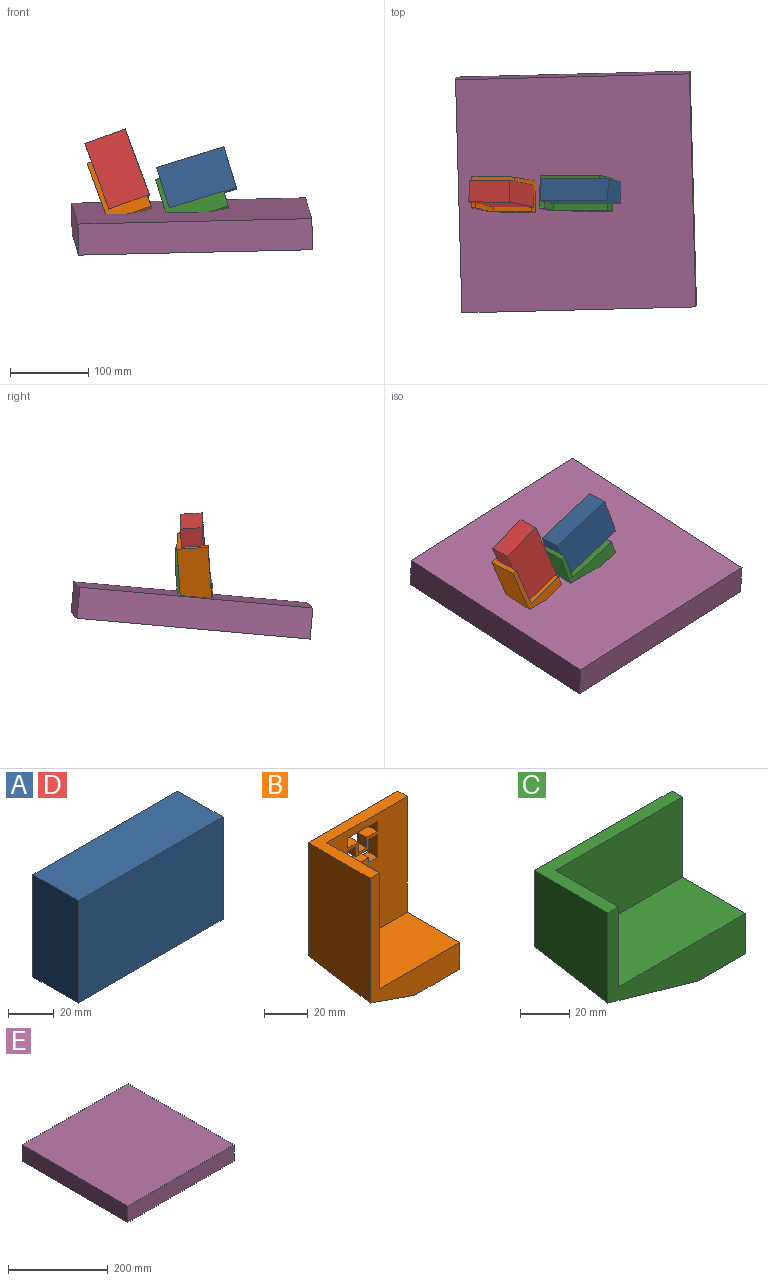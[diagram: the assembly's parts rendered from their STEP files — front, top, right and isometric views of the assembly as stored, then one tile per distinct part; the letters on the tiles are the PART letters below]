
ASSEMBLY  parts=5 mates=4
PART A: 6 faces, bbox 90x28x55 mm
  f0: plane 90x28mm, normal (0,0,1), area 2520mm2, adj f1,f3,f4,f5
  f1: plane 55x28mm, normal (-1,0,0), area 1540mm2, adj f0,f2,f4,f5
  f2: plane 90x28mm, normal (0,0,-1), area 2520mm2, adj f1,f3,f4,f5
  f3: plane 55x28mm, normal (1,0,0), area 1540mm2, adj f0,f2,f4,f5
  f4: plane 90x55mm, normal (0,-1,0), area 4950mm2, adj f0,f1,f2,f3
  f5: plane 90x55mm, normal (0,1,0), area 4950mm2, adj f0,f1,f2,f3
PART B: 30 faces, bbox 58x40x80 mm
  f0: plane 80x58mm, normal (0,1,0), area 3928.8mm2, adj f3,f4,f5,f6,f9,f10,f11,f12
  f1: plane 65x52mm, normal (0,-1,0), area 3062.6mm2, adj f5,f6,f7,f8,f10,f11,f12,f13
  f2: plane 80x58mm, normal (0,-1,0), area 1114.5mm2, adj f3,f4,f5,f6,f7,f8,f9
  f3: plane 69.92x40mm, normal (-1,0,0), area 2666.6mm2, adj f0,f2,f6,f9
  f4: plane 40x29.14mm, normal (0,0,-1), area 793mm2, adj f0,f2,f5,f9
  f5: plane 80x40mm, normal (1,0,0), area 990mm2, adj f0,f1,f2,f4,f6,f8
  f6: plane 58x40mm, normal (0,0,1), area 552mm2, adj f0,f1,f2,f3,f5,f7
  f7: plane 65x34mm, normal (1,0,0), area 2210mm2, adj f1,f2,f6,f8
  f8: plane 52x34mm, normal (0,0,1), area 1768mm2, adj f1,f2,f5,f7
  f9: plane 47.49x40mm, normal (-0.33,0.15,-0.93), area 1636.4mm2, adj f0,f2,f3,f4
  f10: plane 6x5.37mm, normal (0,0,-1), area 32.2mm2, adj f0,f1,f11,f21
  f11: plane 12.91x6mm, normal (-1,0,0), area 77.5mm2, adj f0,f1,f10,f12
  f12: plane 6x5.37mm, normal (0,0,1), area 32.2mm2, adj f0,f1,f11,f13
  f13: plane 6x2.4mm, normal (1,0,0), area 14.4mm2, adj f0,f1,f12,f14
  f14: plane 8.43x6mm, normal (0,0,1), area 50.6mm2, adj f0,f1,f13,f15
  f15: plane 6x2.4mm, normal (-1,0,0), area 14.4mm2, adj f0,f1,f14,f16
  f16: plane 6x5.37mm, normal (0,0,1), area 32.2mm2, adj f0,f1,f15,f17
  f17: plane 12.91x6mm, normal (1,0,0), area 77.5mm2, adj f0,f1,f16,f18
  f18: plane 6x5.37mm, normal (0,0,-1), area 32.2mm2, adj f0,f1,f17,f19
  f19: plane 6x5.8mm, normal (-1,0,0), area 34.8mm2, adj f0,f1,f18,f20
  f20: plane 8.43x6mm, normal (0,0,-1), area 50.6mm2, adj f0,f1,f19,f21
  f21: plane 6x5.8mm, normal (1,0,0), area 34.8mm2, adj f0,f1,f10,f20
  f22: plane 6x5.67mm, normal (-1,0,0), area 34mm2, adj f0,f1,f23,f27
  f23: plane 6.97x6mm, normal (0,0,1), area 41.8mm2, adj f0,f1,f22,f24
  f24: plane 6x5.8mm, normal (-1,0,0), area 34.8mm2, adj f0,f1,f23,f25
  f25: plane 6x5.23mm, normal (0,0,1), area 31.4mm2, adj f0,f1,f24,f26
  f26: plane 6x5.8mm, normal (1,0,0), area 34.8mm2, adj f0,f1,f25,f28
  f27: plane 19.17x6mm, normal (0,0,-1), area 115mm2, adj f0,f1,f22,f29
  f28: plane 6.97x6mm, normal (0,0,1), area 41.8mm2, adj f0,f1,f26,f29
  f29: plane 6x5.67mm, normal (1,0,0), area 34mm2, adj f0,f1,f27,f28
PART C: 10 faces, bbox 79.2x42.3x60 mm
  f0: plane 79.22x60mm, normal (0,1,0), area 3914mm2, adj f1,f3,f4,f5,f9
  f1: plane 45x42.31mm, normal (-1,0,0), area 1755.9mm2, adj f0,f2,f5,f9
  f2: plane 79.22x60mm, normal (0,-1,0), area 1434.3mm2, adj f1,f3,f4,f5,f7,f8,f9
  f3: plane 42.31x27.22mm, normal (0,0,-1), area 638.2mm2, adj f0,f2,f4,f9
  f4: plane 60x42.31mm, normal (1,0,0), area 1086.2mm2, adj f0,f2,f3,f5,f6,f8
  f5: plane 79.22x42.31mm, normal (0,0,1), area 693.2mm2, adj f0,f1,f2,f4,f6,f7
  f6: plane 73.22x40mm, normal (0,-1,0), area 2928.6mm2, adj f4,f5,f7,f8
  f7: plane 40x36.31mm, normal (1,0,0), area 1452.4mm2, adj f2,f5,f6,f8
  f8: plane 73.22x36.31mm, normal (0,0,1), area 2658.5mm2, adj f2,f4,f6,f7
  f9: plane 76.27x42.31mm, normal (-0.27,0.16,-0.95), area 2859.6mm2, adj f0,f1,f2,f3
PART D: same geometry as A
PART E: 6 faces, bbox 300x300x40 mm
  f0: plane 300x40mm, normal (0,1,0), area 12000mm2, adj f1,f3,f4,f5
  f1: plane 300x40mm, normal (-1,0,0), area 12000mm2, adj f0,f2,f4,f5
  f2: plane 300x40mm, normal (0,-1,0), area 12000mm2, adj f1,f3,f4,f5
  f3: plane 300x40mm, normal (1,0,0), area 12000mm2, adj f0,f2,f4,f5
  f4: plane 300x300mm, normal (0,0,-1), area 90000mm2, adj f0,f1,f2,f3
  f5: plane 300x300mm, normal (0,0,1), area 90000mm2, adj f0,f1,f2,f3
PLACE A rot(axis=(-0.23,-0.97,-0.03),17.6deg) t=(-121.18,-44.65,-82.41)mm
PLACE B rot(axis=(-0.18,-0.98,-0.05),20.6deg) t=(-162.11,-86.2,-74.05)mm
PLACE C rot(axis=(-0.23,-0.97,-0.03),17.6deg) t=(-33.56,-59.33,-62.96)mm
PLACE D rot(axis=(-0.04,-1,0.02),110.3deg) t=(-73.11,-51.47,-81.82)mm
PLACE E rot(axis=(0.93,-0.23,0.28),5.5deg) t=(-48.14,-58.36,-57.71)mm
MATE fastened B.f9 <-> E.f5  axis (0.02,0.09,-1) through (-138.08,-60.65,-59.78)mm
MATE fastened C.f9 <-> E.f5  axis (0.02,0.09,-1) through (-48.14,-58.36,-57.71)mm
MATE fastened C.f6 <-> A.f5  axis (-0.02,-1,0.07) through (-76.25,-43.82,-56.3)mm
MATE fastened D.f5 <-> B.f1  axis (0.03,1,-0.06) through (-153.2,-47.68,-57.54)mm
